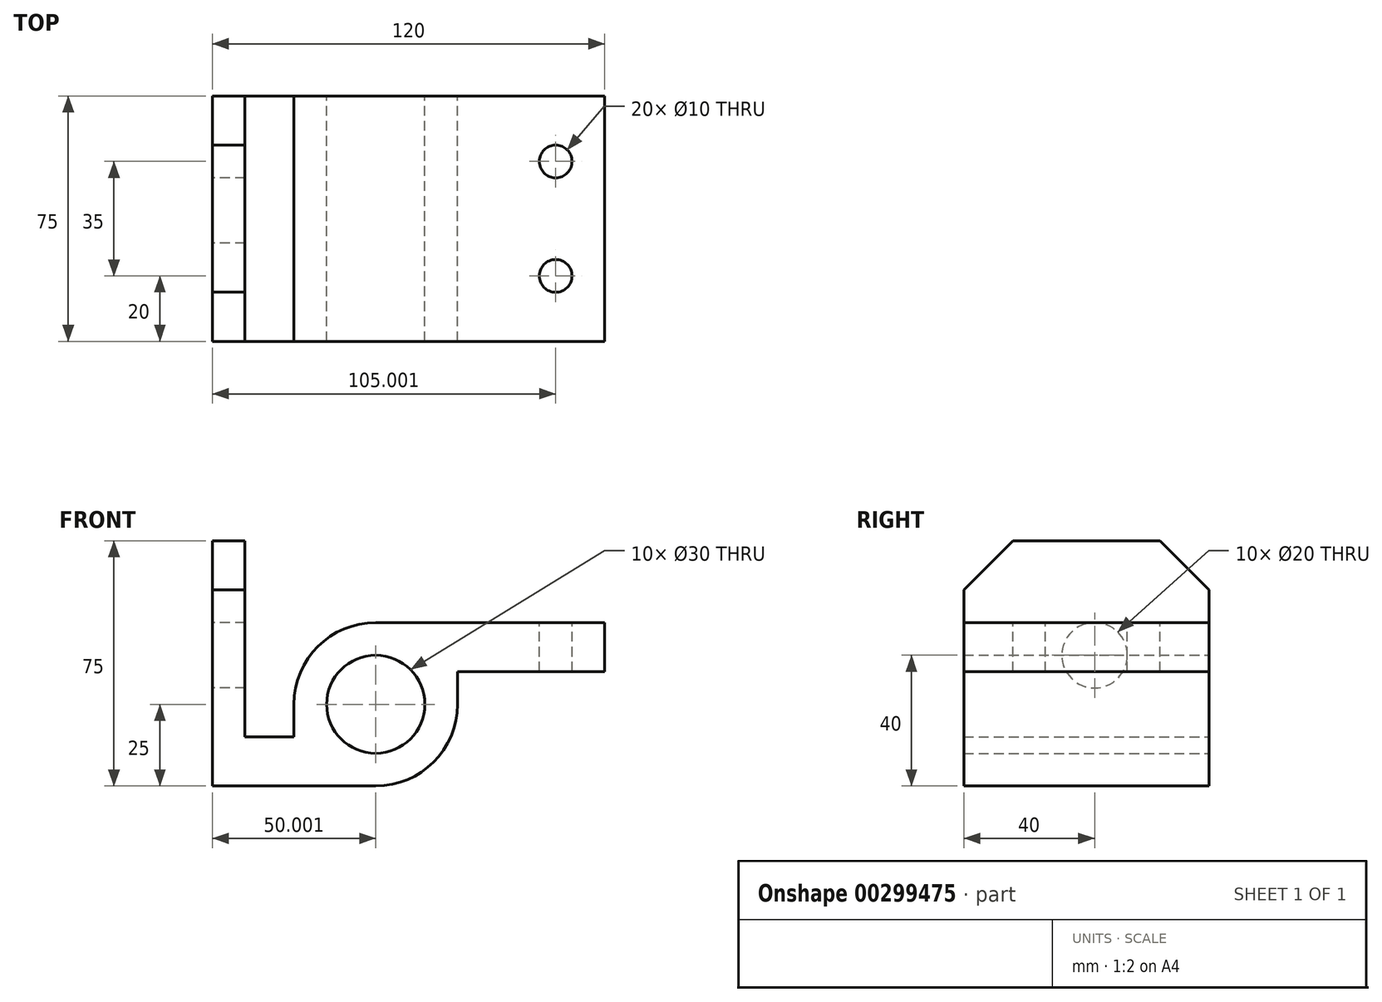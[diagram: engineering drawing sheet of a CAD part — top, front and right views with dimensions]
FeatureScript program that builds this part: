
annotation { "Feature Type Name" : "Feature", "Feature Type Description" : "" }
export const myFeature = defineFeature(function(context is Context, id is Id, definition is map)
    precondition{}
    {
        {
            var Q0;
            Q0=qCreatedBy(makeId("Front.planeOp"),FACE);
            var sketch = newSketch(context, id + "F0", { "sketchPlane" : qUnion([Q0])});
            skLineSegment(sketch, "E0.bottom", {"start": v(-88.53, -25) * mm, "end": v(-38.53, -25) * mm});
            skLineSegment(sketch, "E0.top", {"start": v(-88.53, 50) * mm, "end": v(31.47, 50) * mm});
            skLineSegment(sketch, "E0.left", {"start": v(-88.53, -25) * mm, "end": v(-88.53, 50) * mm});
            skLineSegment(sketch, "E0.right", {"start": v(31.47, -25) * mm, "end": v(31.47, 50) * mm});
            skLineSegment(sketch, "E1.bottom", {"start": v(-78.53, 50) * mm, "end": v(-53.82, 50) * mm});
            skLineSegment(sketch, "E1.top", {"start": v(-78.53, -10) * mm, "end": v(-63.53, -10) * mm});
            skLineSegment(sketch, "E1.left", {"start": v(-78.53, 50) * mm, "end": v(-78.53, -10) * mm});
            skLineSegment(sketch, "E1.right", {"start": v(-63.53, 0) * mm, "end": v(-63.53, -10) * mm});
            skLineSegment(sketch, "E2.bottom", {"start": v(-53.82, 50) * mm, "end": v(31.47, 50) * mm});
            skLineSegment(sketch, "E2.top", {"start": v(-38.53, 25) * mm, "end": v(31.47, 25) * mm});
            skLineSegment(sketch, "E2.left", {"start": v(-53.82, 50) * mm, "end": v(-53.82, 39.72) * mm});
            skLineSegment(sketch, "E2.right", {"start": v(31.47, 50) * mm, "end": v(31.47, 25) * mm});
            skLineSegment(sketch, "E3.bottom", {"start": v(-13.53, -25) * mm, "end": v(31.47, -25) * mm});
            skLineSegment(sketch, "E3.top", {"start": v(-13.53, 10) * mm, "end": v(31.47, 10) * mm});
            skLineSegment(sketch, "E3.left", {"start": v(-13.53, 0) * mm, "end": v(-13.53, 10) * mm});
            skLineSegment(sketch, "E3.right", {"start": v(31.47, -25) * mm, "end": v(31.47, 10) * mm});
            skCircle(sketch, "E4", {"center": v(-38.53, 0) * mm, "radius": 15 * mm});
            skArc(sketch, "E5.filletArc", {"start": v(-38.53, 25) * mm, "mid": v(-56.2, 17.68) * mm, "end": v(-63.53, 0) * mm});
            skPoint(sketch, "E6.newPointB", {"position": v(31.47, -25) * mm});
            skArc(sketch, "E6.filletArc", {"start": v(-38.53, -25) * mm, "mid": v(-20.85, -17.68) * mm, "end": v(-13.53, 0) * mm});
            skSolve(sketch);
        }
        {
            var Q0;
            Q0=makeQuery(id+"F0.imprint","IMPRINT",FACE,{"disambiguationData":[TD([[makeQuery(id+"F0.imprint","IMPRINT",EDGE,{"derivedFrom":sQuery(id+"F0.wireOp",EDGE,"E0.bottom")}),1.0]])]});
            extrude(context, id + "F1", {"entities" : qUnion([Q0]), "depth" : 75 * mm});
        }
        {
            var Q0;
            Q0=makeQuery(id+"F1.opExtrude","SWEPT_FACE",FACE,{"disambiguationData":[OSD([sQuery(id+"F0.wireOp",EDGE,"E0.left")])]});
            var sketch = newSketch(context, id + "F2", { "sketchPlane" : qUnion([Q0])});
            skLineSegment(sketch, "E7", {"start": v(15, 50) * mm, "end": v(0, 35) * mm});
            skLineSegment(sketch, "E8", {"start": v(60, 50) * mm, "end": v(75, 35) * mm});
            skCircle(sketch, "E9", {"center": v(35, 15) * mm, "radius": 10 * mm});
            skSolve(sketch);
        }
        {
            var Q0;
            {var subQ0=sQuery(id+"F2.wireOp",EDGE,"E7");Q0=makeQuery(id+"F2.imprint","IMPRINT",FACE,{"disambiguationData":[TD([[makeQuery(id+"F2.imprint","IMPRINT",EDGE,{"derivedFrom":subQ0}),-1.0]])]});}
            var Q1;
            {var subQ0=sQuery(id+"F2.wireOp",EDGE,"E8");Q1=makeQuery(id+"F2.imprint","IMPRINT",FACE,{"disambiguationData":[TD([[makeQuery(id+"F2.imprint","IMPRINT",EDGE,{"derivedFrom":subQ0}),1.0]])]});}
            var Q2;
            Q2=makeQuery(id+"F2.imprint","IMPRINT",FACE,{"disambiguationData":[TD([[makeQuery(id+"F2.imprint","IMPRINT",EDGE,{"derivedFrom":sQuery(id+"F2.wireOp",EDGE,"E9")}),1.0]])]});
            extrude(context, id + "F3", {"entities" : qUnion([Q0, Q1, Q2]), "operationType" : NewBodyOperationType.REMOVE, "oppositeDirection" : true, "depth" : 10 * mm});
        }
        {
            var Q0;
            Q0=makeQuery(id+"F1.opExtrude","SWEPT_FACE",FACE,{"disambiguationData":[OSD([sQuery(id+"F0.wireOp",EDGE,"E2.top")])]});
            var sketch = newSketch(context, id + "F4", { "sketchPlane" : qUnion([Q0])});
            skCircle(sketch, "E10", {"center": v(16.47, -20) * mm, "radius": 5 * mm});
            skCircle(sketch, "E11", {"center": v(16.47, -55) * mm, "radius": 5 * mm});
            skSolve(sketch);
        }
        {
            var Q0;
            Q0=makeQuery(id+"F4.imprint","IMPRINT",FACE,{"disambiguationData":[TD([[makeQuery(id+"F4.imprint","IMPRINT",EDGE,{"derivedFrom":sQuery(id+"F4.wireOp",EDGE,"E10")}),1.0]])]});
            var Q1;
            Q1=makeQuery(id+"F4.imprint","IMPRINT",FACE,{"disambiguationData":[TD([[makeQuery(id+"F4.imprint","IMPRINT",EDGE,{"derivedFrom":sQuery(id+"F4.wireOp",EDGE,"E11")}),1.0]])]});
            extrude(context, id + "F5", {"entities" : qUnion([Q0, Q1]), "operationType" : NewBodyOperationType.REMOVE, "oppositeDirection" : true, "depth" : 15 * mm});
        }
    });
